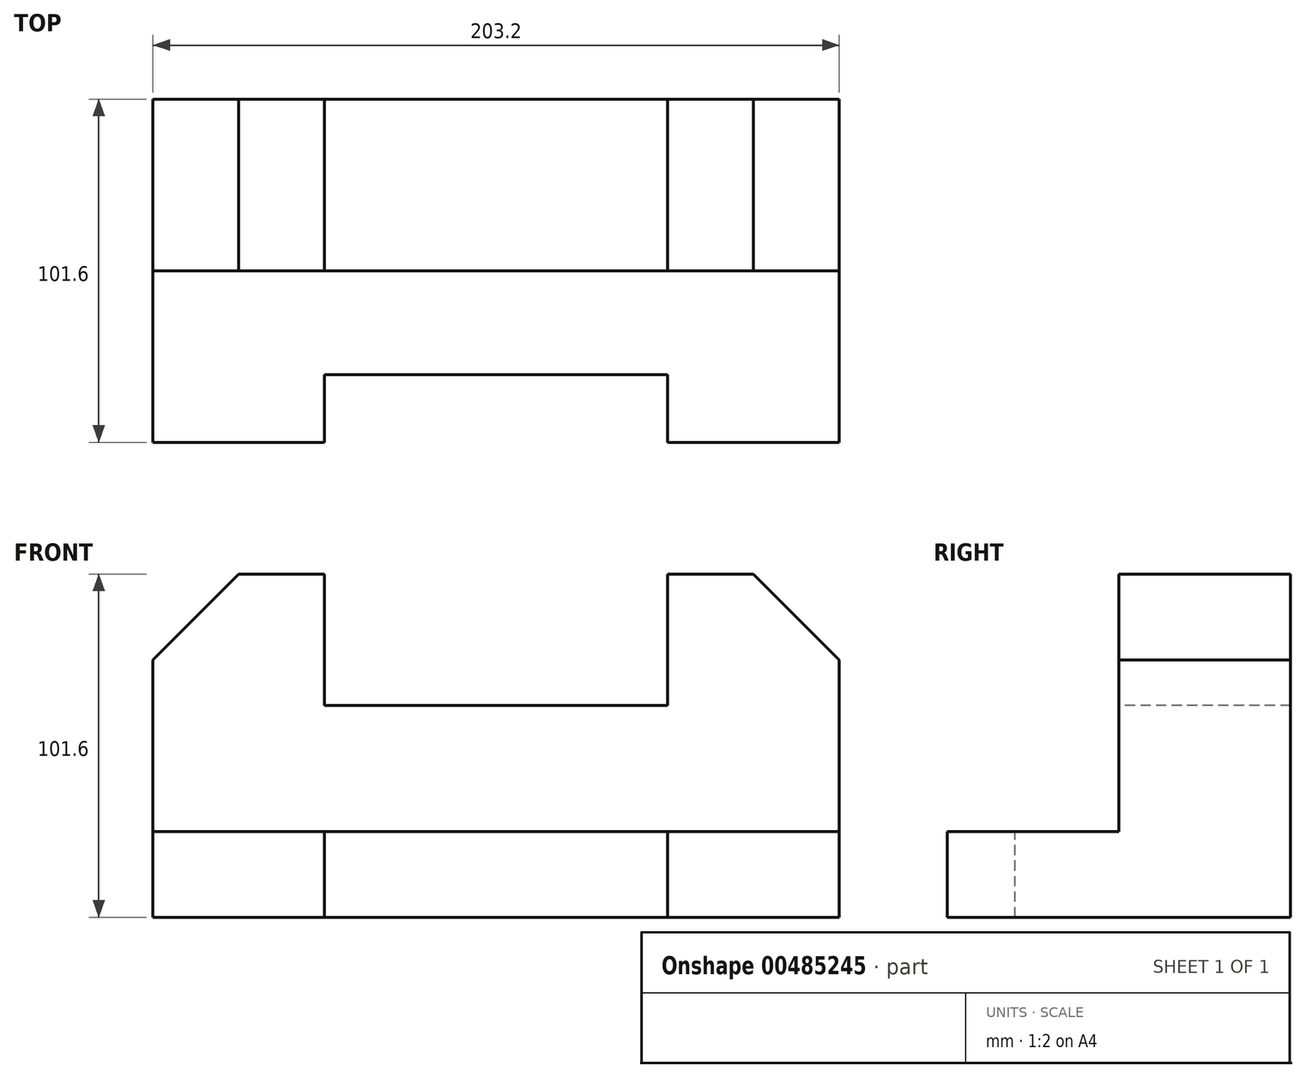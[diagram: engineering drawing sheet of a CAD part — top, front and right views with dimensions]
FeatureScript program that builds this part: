
annotation { "Feature Type Name" : "Feature", "Feature Type Description" : "" }
export const myFeature = defineFeature(function(context is Context, id is Id, definition is map)
    precondition{}
    {
        {
            var Q0;
            Q0=qCreatedBy(makeId("Front.planeOp"),FACE);
            var sketch = newSketch(context, id + "F0", { "sketchPlane" : qUnion([Q0])});
            skLineSegment(sketch, "E0.bottom", {"start": v(-101.6, 59.03) * mm, "end": v(101.6, 59.03) * mm});
            skLineSegment(sketch, "E0.top", {"start": v(-101.6, -42.57) * mm, "end": v(101.6, -42.57) * mm});
            skLineSegment(sketch, "E0.left", {"start": v(-101.6, 59.03) * mm, "end": v(-101.6, -42.57) * mm});
            skLineSegment(sketch, "E0.right", {"start": v(101.6, 59.03) * mm, "end": v(101.6, -42.57) * mm});
            skLineSegment(sketch, "E1.bottom", {"start": v(-50.8, 59.03) * mm, "end": v(50.8, 59.03) * mm});
            skLineSegment(sketch, "E1.top", {"start": v(-50.8, 16.91) * mm, "end": v(50.8, 16.91) * mm});
            skLineSegment(sketch, "E1.left", {"start": v(-50.8, 59.03) * mm, "end": v(-50.8, 16.91) * mm});
            skLineSegment(sketch, "E1.right", {"start": v(50.8, 59.03) * mm, "end": v(50.8, 16.91) * mm});
            skSolve(sketch);
        }
        {
            var Q0;
            Q0 = qSketchRegion(id + "F0", true);
            extrude(context, id + "F1", {"entities" : qUnion([Q0]), "depth" : 101.6 * mm});
        }
        {
            var Q0;
            Q0=makeQuery(id+"F1.opExtrude","SWEPT_FACE",FACE,{"disambiguationData":[OSD([sQuery(id+"F0.wireOp",EDGE,"E0.right")])]});
            var sketch = newSketch(context, id + "F2", { "sketchPlane" : qUnion([Q0])});
            skLineSegment(sketch, "E2.bottom", {"start": v(-101.6, 59.03) * mm, "end": v(-50.8, 59.03) * mm});
            skLineSegment(sketch, "E2.top", {"start": v(-101.6, -17.17) * mm, "end": v(-50.8, -17.17) * mm});
            skLineSegment(sketch, "E2.left", {"start": v(-101.6, 59.03) * mm, "end": v(-101.6, -17.17) * mm});
            skLineSegment(sketch, "E2.right", {"start": v(-50.8, 59.03) * mm, "end": v(-50.8, -17.17) * mm});
            skSolve(sketch);
        }
        {
            var Q0;
            Q0 = qSketchRegion(id + "F2", true);
            extrude(context, id + "F3", {"entities" : qUnion([Q0]), "operationType" : NewBodyOperationType.REMOVE, "oppositeDirection" : true, "depth" : 203.2 * mm});
        }
        {
            var Q0;
            Q0=makeQuery(id+"F3.boolean.opBoolean","COPY",FACE,{"derivedFrom":makeQuery(id+"F3.opExtrude","SWEPT_FACE",FACE,{"disambiguationData":[OSD([sQuery(id+"F2.wireOp",EDGE,"E2.top")])]})});
            var sketch = newSketch(context, id + "F4", { "sketchPlane" : qUnion([Q0])});
            skLineSegment(sketch, "E3.bottom", {"start": v(-50.8, -101.6) * mm, "end": v(50.8, -101.6) * mm});
            skLineSegment(sketch, "E3.top", {"start": v(-50.8, -81.6) * mm, "end": v(50.8, -81.6) * mm});
            skLineSegment(sketch, "E3.left", {"start": v(-50.8, -101.6) * mm, "end": v(-50.8, -81.6) * mm});
            skLineSegment(sketch, "E3.right", {"start": v(50.8, -101.6) * mm, "end": v(50.8, -81.6) * mm});
            skSolve(sketch);
        }
        {
            var Q0;
            Q0 = qSketchRegion(id + "F4", true);
            extrude(context, id + "F5", {"entities" : qUnion([Q0]), "operationType" : NewBodyOperationType.REMOVE, "oppositeDirection" : true, "depth" : 25.4 * mm});
        }
        {
            var Q0;
            Q0=makeQuery(id+"F3.boolean.opBoolean","COPY",FACE,{"derivedFrom":makeQuery(id+"F3.opExtrude","SWEPT_FACE",FACE,{"disambiguationData":[OSD([sQuery(id+"F2.wireOp",EDGE,"E2.right")])]})});
            var sketch = newSketch(context, id + "F6", { "sketchPlane" : qUnion([Q0])});
            skLineSegment(sketch, "E4.bottom", {"start": v(-50.8, 59.03) * mm, "end": v(50.8, 59.03) * mm});
            skLineSegment(sketch, "E4.top", {"start": v(-50.8, 20.07) * mm, "end": v(50.8, 20.07) * mm});
            skLineSegment(sketch, "E4.left", {"start": v(-50.8, 59.03) * mm, "end": v(-50.8, 20.07) * mm});
            skLineSegment(sketch, "E4.right", {"start": v(50.8, 59.03) * mm, "end": v(50.8, 20.07) * mm});
            skSolve(sketch);
        }
        {
            var Q0;
            Q0=makeQuery(id+"F6.imprint","IMPRINT",FACE,{"disambiguationData":[TD([[makeQuery(id+"F6.imprint","IMPRINT",EDGE,{"derivedFrom":sQuery(id+"F6.wireOp",EDGE,"E4.bottom")}),-1.0]])]});
            extrude(context, id + "F7", {"entities" : qUnion([Q0]), "operationType" : NewBodyOperationType.REMOVE, "oppositeDirection" : true, "depth" : 50.8 * mm});
        }
        {
            var Q0;
            Q0=makeQuery(id+"F3.boolean.opBoolean","COPY",FACE,{"derivedFrom":makeQuery(id+"F3.opExtrude","SWEPT_FACE",FACE,{"disambiguationData":[OSD([sQuery(id+"F2.wireOp",EDGE,"E2.right")])]})});
            var sketch = newSketch(context, id + "F8", { "sketchPlane" : qUnion([Q0])});
            skLineSegment(sketch, "E5", {"start": v(-101.6, 59.03) * mm, "end": v(-101.6, 33.63) * mm});
            skLineSegment(sketch, "E6", {"start": v(-101.6, 33.63) * mm, "end": v(-76.2, 59.03) * mm});
            skLineSegment(sketch, "E7", {"start": v(-76.2, 59.03) * mm, "end": v(-101.6, 59.03) * mm});
            skSolve(sketch);
        }
        {
            var Q0;
            Q0 = qSketchRegion(id + "F8", true);
            extrude(context, id + "F9", {"entities" : qUnion([Q0]), "operationType" : NewBodyOperationType.REMOVE, "oppositeDirection" : true, "depth" : 101.6 * mm});
        }
        {
            var Q0;
            Q0=makeQuery(id+"F3.boolean.opBoolean","COPY",FACE,{"derivedFrom":makeQuery(id+"F3.opExtrude","SWEPT_FACE",FACE,{"disambiguationData":[OSD([sQuery(id+"F2.wireOp",EDGE,"E2.right")])]})});
            var sketch = newSketch(context, id + "F10", { "sketchPlane" : qUnion([Q0])});
            skLineSegment(sketch, "E8", {"start": v(101.6, 33.63) * mm, "end": v(101.6, 59.03) * mm});
            skLineSegment(sketch, "E9", {"start": v(101.6, 59.03) * mm, "end": v(76.2, 59.03) * mm});
            skLineSegment(sketch, "E10", {"start": v(76.2, 59.03) * mm, "end": v(101.6, 33.63) * mm});
            skSolve(sketch);
        }
        {
            var Q0;
            Q0 = qSketchRegion(id + "F10", true);
            extrude(context, id + "F11", {"entities" : qUnion([Q0]), "operationType" : NewBodyOperationType.REMOVE, "oppositeDirection" : true, "depth" : 101.6 * mm});
        }
    });
